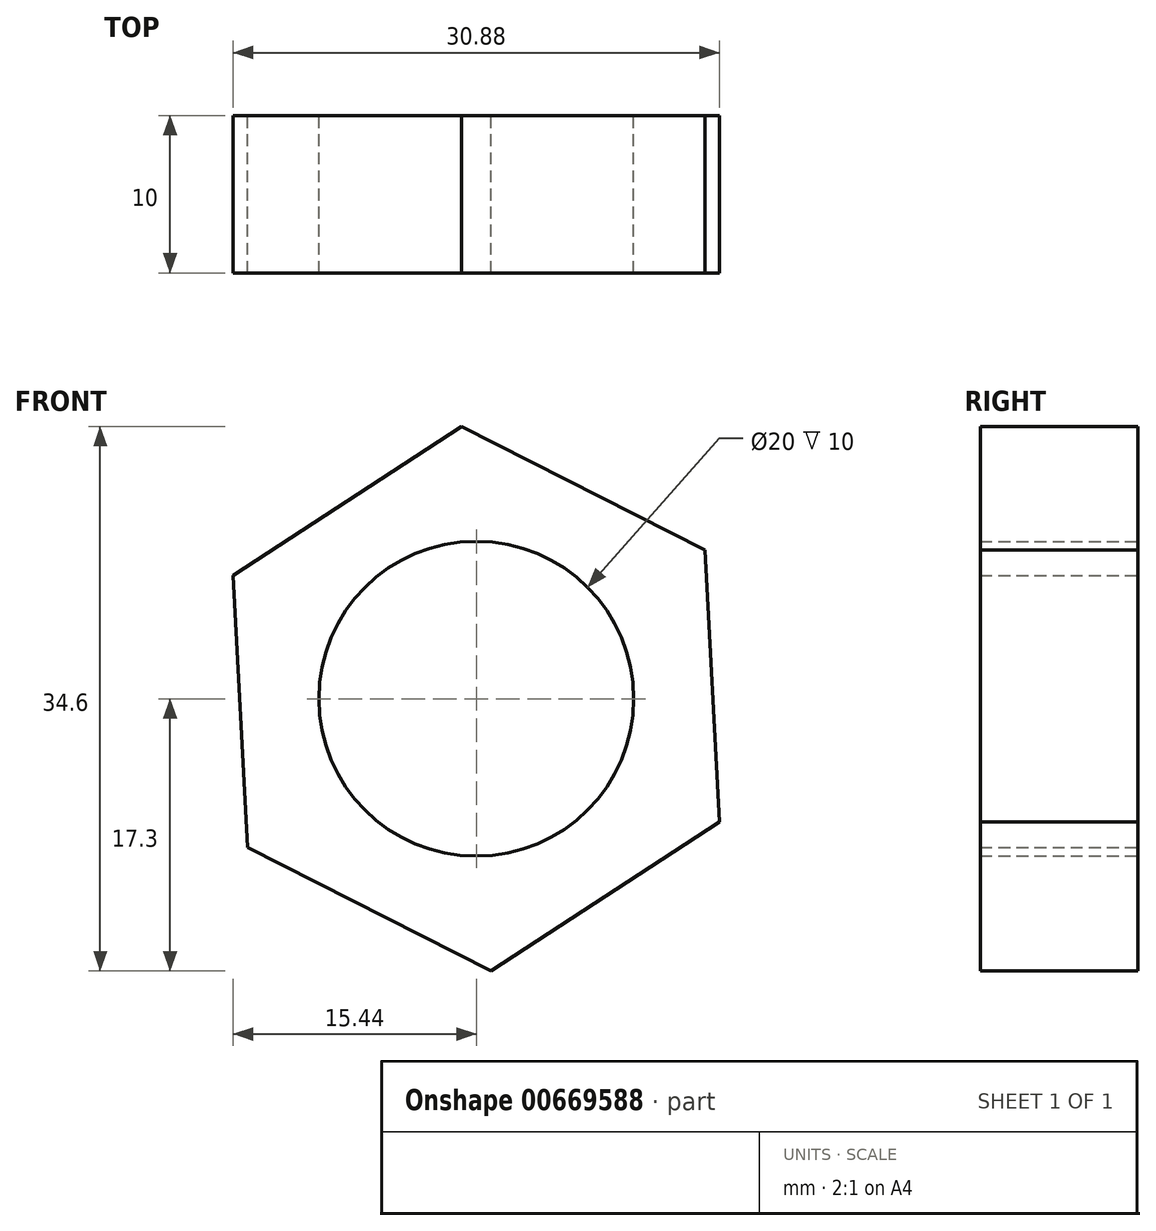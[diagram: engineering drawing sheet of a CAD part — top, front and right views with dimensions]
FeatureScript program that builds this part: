
annotation { "Feature Type Name" : "Feature", "Feature Type Description" : "" }
export const myFeature = defineFeature(function(context is Context, id is Id, definition is map)
    precondition{}
    {
        {
            var Q0;
            Q0=qCreatedBy(makeId("Front.planeOp"),FACE);
            var sketch = newSketch(context, id + "F0", { "sketchPlane" : qUnion([Q0])});
            skCircle(sketch, "E0.cCircle", {"center": v(0, 0) * mm, "radius": 15 * mm, "construction": true});
            skLineSegment(sketch, "E0.0", {"start": v(-15.44, 7.84) * mm, "end": v(-0.93, 17.3) * mm});
            skLineSegment(sketch, "E0.1", {"start": v(-0.93, 17.3) * mm, "end": v(14.51, 9.45) * mm});
            skLineSegment(sketch, "E0.2", {"start": v(14.51, 9.45) * mm, "end": v(15.44, -7.84) * mm});
            skLineSegment(sketch, "E0.3", {"start": v(15.44, -7.84) * mm, "end": v(0.93, -17.3) * mm});
            skLineSegment(sketch, "E0.4", {"start": v(0.93, -17.3) * mm, "end": v(-14.51, -9.45) * mm});
            skLineSegment(sketch, "E0.5", {"start": v(-14.51, -9.45) * mm, "end": v(-15.44, 7.84) * mm});
            skPoint(sketch, "E0.0.midPoint", {"position": v(-8.19, 12.57) * mm});
            skCircle(sketch, "E1", {"center": v(0, 0) * mm, "radius": 10 * mm});
            skSolve(sketch);
        }
        {
            var Q0;
            Q0=makeQuery(id+"F0.imprint","IMPRINT",FACE,{"disambiguationData":[TD([[makeQuery(id+"F0.imprint","IMPRINT",EDGE,{"derivedFrom":sQuery(id+"F0.wireOp",EDGE,"E0.0")}),-1.0]])]});
            extrude(context, id + "F1", {"entities" : qUnion([Q0]), "depth" : 10 * mm, "offsetDistance" : 25 * mm});
        }
    });
